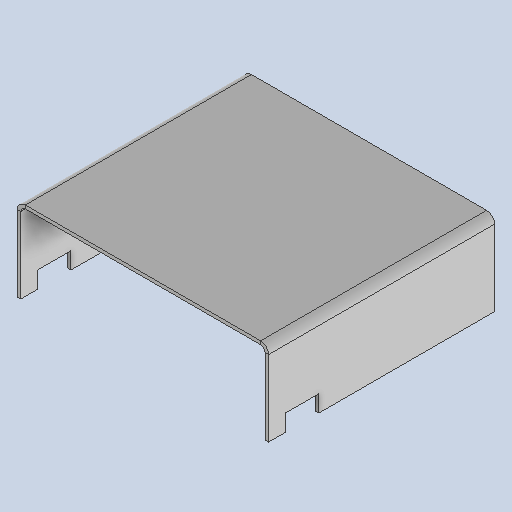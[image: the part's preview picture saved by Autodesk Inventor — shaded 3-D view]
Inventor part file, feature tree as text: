
AUTODESK INVENTOR PART (.ipt)
format: ipt  version: 2025 (Build 290162010, 162A)  size: 279,552 bytes
history: native  units: mm
features: sheet_metal_op x4, sketch x3, other x3, extrude x1, projected_geometry x1
ambient origin geometry x8: Origin, YZ Plane, XZ Plane, XY Plane, X Axis, Y Axis, Z Axis, Center Point
bodies: Solid1 (feature_tree)
feature tree (12):
  sheet_metal_op  "Face1"
  sheet_metal_op  "Flange1"
  extrude  "Extrusion1"  Depth=135.0mm
  sketch  "Sketch1"  dims[d0=150.0mm d1=135.0mm]
  other  "Plate1"
  sketch  "Sketch2"  dims[d2=2.0mm]
  other  "Plate2"
  sheet_metal_op  "Bend1"
  sheet_metal_op  "Corner1"
  sketch  "Sketch3"  dims[d3=2.0mm d4=1.0mm d5=4.0mm d6=2.0mm d7=50.0mm d8=90.0deg d9=2.75mm d10=8.0mm d11=2.0mm d12=2.0mm d13=20.0mm d14=10.0mm d15=0.0mm d16=0.0mm d17=10.0mm]
  projected_geometry  "Projected Loop1"
  other  "Definition1"
